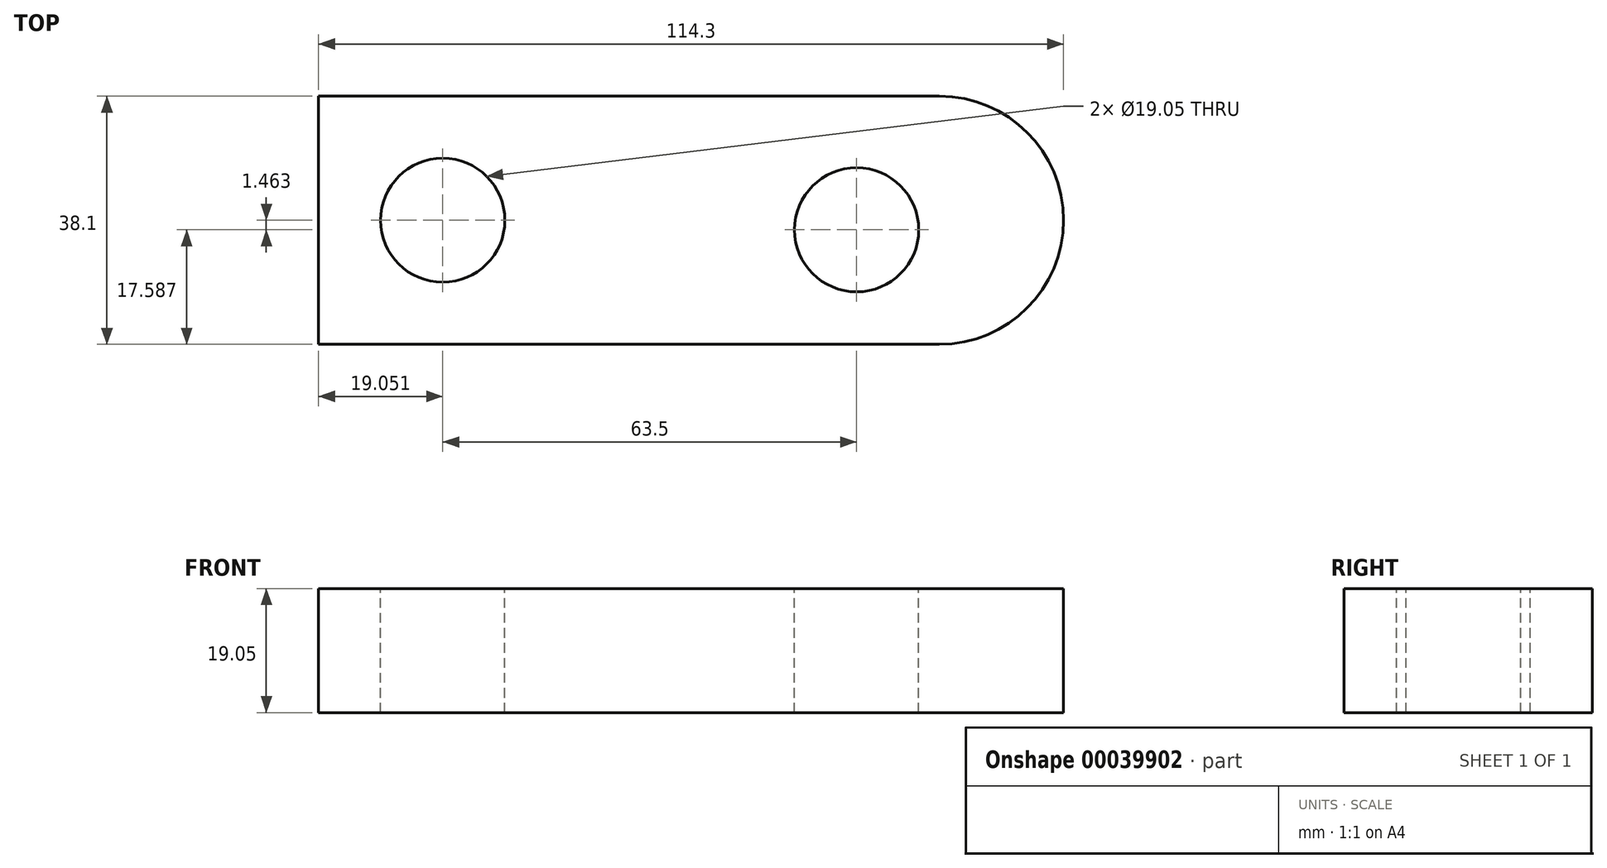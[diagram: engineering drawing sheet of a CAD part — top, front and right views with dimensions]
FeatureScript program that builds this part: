
annotation { "Feature Type Name" : "Feature", "Feature Type Description" : "" }
export const myFeature = defineFeature(function(context is Context, id is Id, definition is map)
    precondition{}
    {
        {
            var Q0;
            Q0=qCreatedBy(makeId("Front.planeOp"),FACE);
            var sketch = newSketch(context, id + "F0", { "sketchPlane" : qUnion([Q0])});
            skLineSegment(sketch, "E0.bottom", {"start": v(-61.63, 0) * mm, "end": v(52.67, 0) * mm});
            skLineSegment(sketch, "E0.top", {"start": v(-61.63, 19.05) * mm, "end": v(52.67, 19.05) * mm});
            skLineSegment(sketch, "E0.left", {"start": v(-61.63, 0) * mm, "end": v(-61.63, 19.05) * mm});
            skLineSegment(sketch, "E0.right", {"start": v(52.67, 0) * mm, "end": v(52.67, 19.05) * mm});
            skSolve(sketch);
        }
        {
            var Q0;
            Q0=makeQuery(id+"F0.imprint","IMPRINT",FACE,{"disambiguationData":[TD([[makeQuery(id+"F0.imprint","IMPRINT",EDGE,{"derivedFrom":sQuery(id+"F0.wireOp",EDGE,"E0.bottom")}),1.0]])]});
            extrude(context, id + "F1", {"entities" : qUnion([Q0]), "depth" : 38.1 * mm});
        }
        {
            var Q0;
            Q0=makeQuery(id+"F1.opExtrude","CAP_EDGE",EDGE,{"disambiguationData":[OSD([sQuery(id+"F0.wireOp",EDGE,"E0.right")])],"isStart":false});
            var Q1;
            Q1=makeQuery(id+"F1.opExtrude","CAP_EDGE",EDGE,{"disambiguationData":[OSD([sQuery(id+"F0.wireOp",EDGE,"E0.right")])],"isStart":true});
            fillet(context, id + "F2", {"entities" : qUnion([Q0, Q1]), "radius" : 19.05 * mm, "tangentPropagation" : true, "allowEdgeOverflow" : false});
        }
        {
            var Q0;
            Q0=makeQuery(id+"F1.opExtrude","SWEPT_FACE",FACE,{"disambiguationData":[OSD([sQuery(id+"F0.wireOp",EDGE,"E0.top")])]});
            var sketch = newSketch(context, id + "F3", { "sketchPlane" : qUnion([Q0])});
            skCircle(sketch, "E1", {"center": v(-42.58, -19.05) * mm, "radius": 9.53 * mm});
            skCircle(sketch, "E2", {"center": v(20.92, -20.51) * mm, "radius": 9.53 * mm});
            skSolve(sketch);
        }
        {
            var Q0;
            Q0=makeQuery(id+"F3.imprint","IMPRINT",FACE,{"disambiguationData":[TD([[makeQuery(id+"F3.imprint","IMPRINT",EDGE,{"derivedFrom":sQuery(id+"F3.wireOp",EDGE,"E1")}),1.0]])]});
            var Q1;
            Q1=makeQuery(id+"F3.imprint","IMPRINT",FACE,{"disambiguationData":[TD([[makeQuery(id+"F3.imprint","IMPRINT",EDGE,{"derivedFrom":sQuery(id+"F3.wireOp",EDGE,"E2")}),1.0]])]});
            extrude(context, id + "F4", {"entities" : qUnion([Q0, Q1]), "operationType" : NewBodyOperationType.REMOVE, "oppositeDirection" : true, "depth" : 38.1 * mm});
        }
    });
